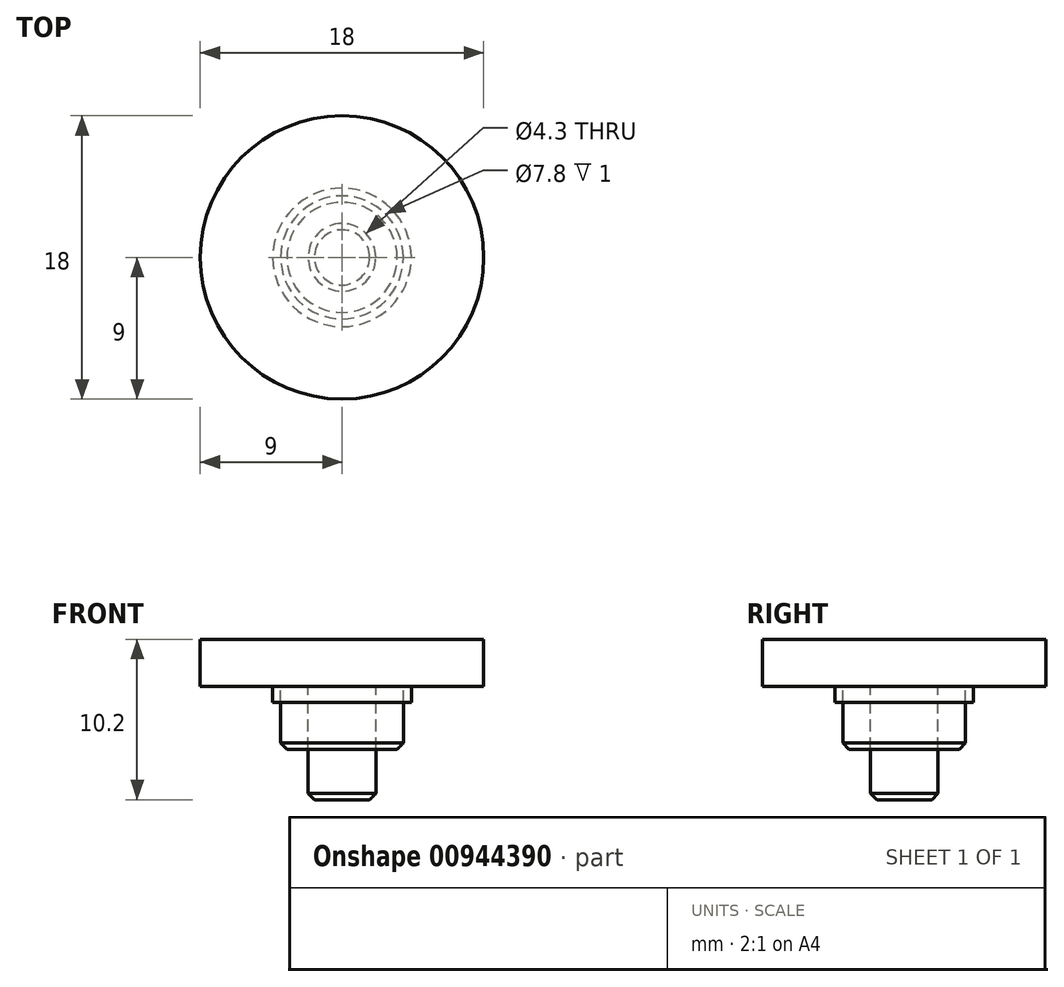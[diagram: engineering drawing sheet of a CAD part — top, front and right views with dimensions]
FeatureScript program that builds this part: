
annotation { "Feature Type Name" : "Feature", "Feature Type Description" : "" }
export const myFeature = defineFeature(function(context is Context, id is Id, definition is map)
    precondition{}
    {
        {
            var Q0;
            Q0=qCreatedBy(makeId("Top.planeOp"),FACE);
            var sketch = newSketch(context, id + "F0", { "sketchPlane" : qUnion([Q0])});
            skCircle(sketch, "E0", {"center": v(0, 0) * mm, "radius": 2.15 * mm});
            skCircle(sketch, "E1", {"center": v(0, 0) * mm, "radius": 3.9 * mm});
            skCircle(sketch, "E2", {"center": v(0, 0) * mm, "radius": 4.4 * mm});
            skCircle(sketch, "E3", {"center": v(0, 0) * mm, "radius": 9 * mm});
            skSolve(sketch);
        }
        {
            var Q0;
            Q0=makeQuery(id+"F0.imprint","IMPRINT",FACE,{"disambiguationData":[TD([[makeQuery(id+"F0.imprint","IMPRINT",EDGE,{"derivedFrom":sQuery(id+"F0.wireOp",EDGE,"E1")}),-1.0]])]});
            extrude(context, id + "F1", {"entities" : qUnion([Q0]), "depth" : -1 * mm, "offsetDistance" : 25 * mm});
        }
        {
            var Q0;
            Q0=makeQuery(id+"F0.imprint","IMPRINT",FACE,{"disambiguationData":[TD([[makeQuery(id+"F0.imprint","IMPRINT",EDGE,{"derivedFrom":sQuery(id+"F0.wireOp",EDGE,"E0")}),-1.0]])]});
            extrude(context, id + "F2", {"entities" : qUnion([Q0]), "depth" : -4 * mm, "offsetDistance" : 25 * mm});
        }
        {
            var Q0;
            Q0=makeQuery(id+"F0.imprint","IMPRINT",FACE,{"disambiguationData":[TD([[makeQuery(id+"F0.imprint","IMPRINT",EDGE,{"derivedFrom":sQuery(id+"F0.wireOp",EDGE,"E0")}),1.0]])]});
            extrude(context, id + "F3", {"entities" : qUnion([Q0]), "depth" : -7.2 * mm, "offsetDistance" : 25 * mm});
        }
        {
            var Q0;
            Q0=makeQuery(id+"F3.opExtrude","CAP_EDGE",EDGE,{"disambiguationData":[OSD([sQuery(id+"F0.wireOp",EDGE,"E0")])],"isStart":false});
            var Q1;
            Q1=makeQuery(id+"F2.opExtrude","CAP_EDGE",EDGE,{"disambiguationData":[OSD([sQuery(id+"F0.wireOp",EDGE,"E1")])],"isStart":false});
            chamfer(context, id + "F4", {"entities" : qUnion([Q0, Q1]), "width" : 0.4 * mm, "tangentPropagation" : true});
        }
        {
            var Q0;
            Q0=makeQuery(id+"F0.imprint","IMPRINT",FACE,{"disambiguationData":[TD([[makeQuery(id+"F0.imprint","IMPRINT",EDGE,{"derivedFrom":sQuery(id+"F0.wireOp",EDGE,"E2")}),-1.0]])]});
            var Q1;
            Q1=makeQuery(id+"F0.imprint","IMPRINT",FACE,{"disambiguationData":[TD([[makeQuery(id+"F0.imprint","IMPRINT",EDGE,{"derivedFrom":sQuery(id+"F0.wireOp",EDGE,"E1")}),-1.0]])]});
            var Q2;
            Q2=makeQuery(id+"F0.imprint","IMPRINT",FACE,{"disambiguationData":[TD([[makeQuery(id+"F0.imprint","IMPRINT",EDGE,{"derivedFrom":sQuery(id+"F0.wireOp",EDGE,"E0")}),-1.0]])]});
            var Q3;
            Q3=makeQuery(id+"F0.imprint","IMPRINT",FACE,{"disambiguationData":[TD([[makeQuery(id+"F0.imprint","IMPRINT",EDGE,{"derivedFrom":sQuery(id+"F0.wireOp",EDGE,"E0")}),1.0]])]});
            extrude(context, id + "F5", {"entities" : qUnion([Q0, Q1, Q2, Q3]), "depth" : 3 * mm, "offsetDistance" : 25 * mm});
        }
    });
